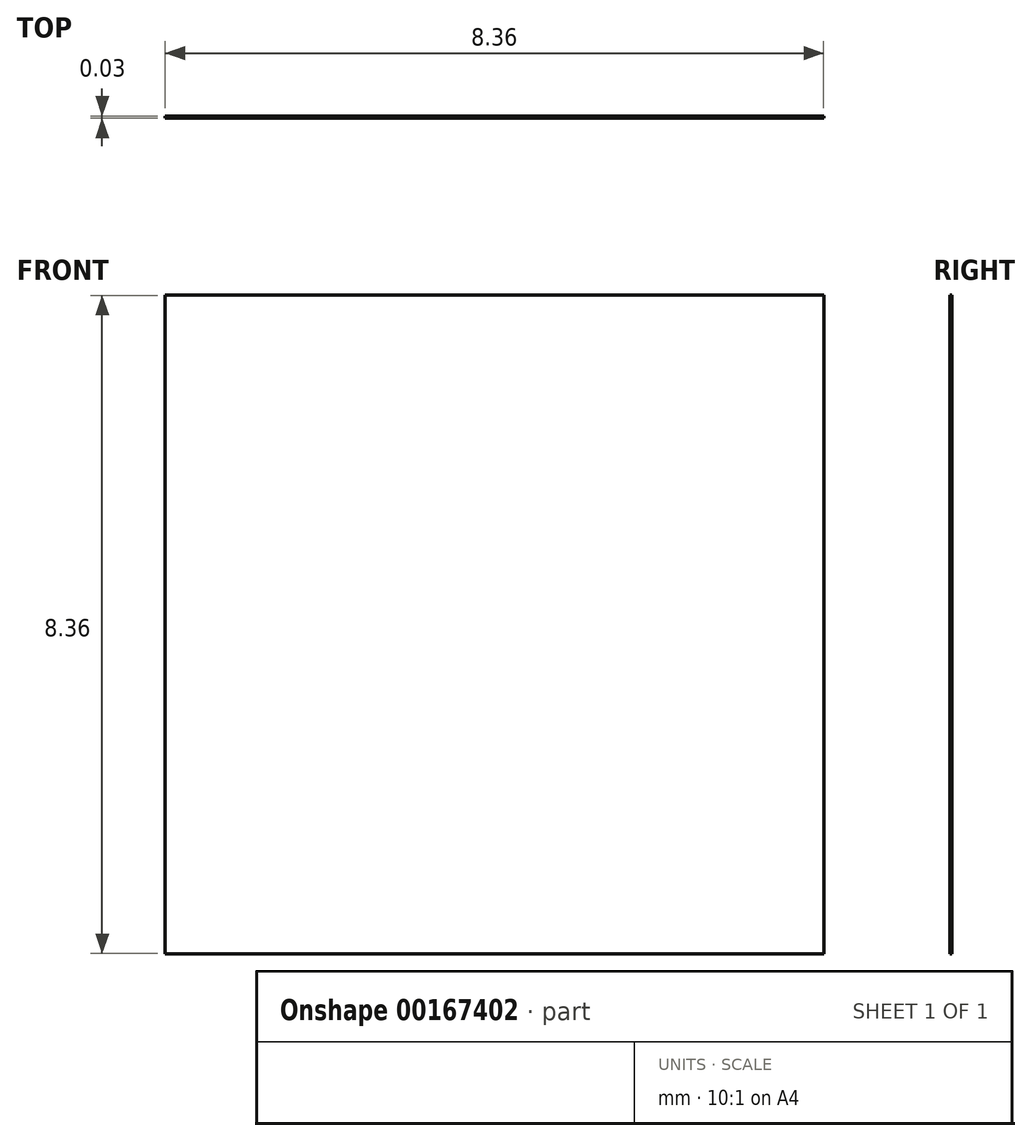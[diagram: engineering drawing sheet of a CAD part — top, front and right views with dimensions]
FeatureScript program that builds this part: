
annotation { "Feature Type Name" : "Feature", "Feature Type Description" : "" }
export const myFeature = defineFeature(function(context is Context, id is Id, definition is map)
    precondition{}
    {
        {
            var Q0;
            Q0=qCreatedBy(makeId("Front.planeOp"),FACE);
            var sketch = newSketch(context, id + "F0", { "sketchPlane" : qUnion([Q0])});
            skLineSegment(sketch, "E0.bottom", {"start": v(4.18, -4.18) * mm, "end": v(-4.18, -4.18) * mm});
            skLineSegment(sketch, "E0.top", {"start": v(4.18, 4.18) * mm, "end": v(-4.18, 4.18) * mm});
            skLineSegment(sketch, "E0.left", {"start": v(4.18, -4.18) * mm, "end": v(4.18, 4.18) * mm});
            skLineSegment(sketch, "E0.right", {"start": v(-4.18, -4.18) * mm, "end": v(-4.18, 4.18) * mm});
            skPoint(sketch, "E0.middle", {"position": v(0, 0) * mm});
            skSolve(sketch);
        }
        {
            var Q0;
            Q0=makeQuery(id+"F0.imprint","IMPRINT",FACE,{"disambiguationData":[TD([[makeQuery(id+"F0.imprint","IMPRINT",EDGE,{"derivedFrom":sQuery(id+"F0.wireOp",EDGE,"E0.bottom")}),-1.0]])]});
            extrude(context, id + "F1", {"entities" : qUnion([Q0]), "depth" : 0.03 * mm});
        }
    });
